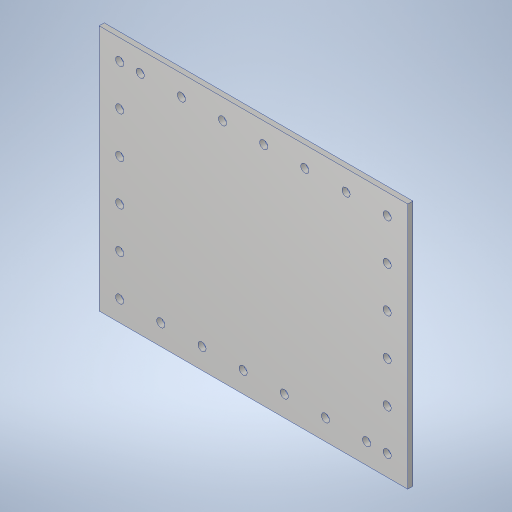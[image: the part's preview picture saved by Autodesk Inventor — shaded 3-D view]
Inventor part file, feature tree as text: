
AUTODESK INVENTOR PART (.ipt)
format: ipt  version: 2023.4 (Build 274418000, 418)  size: 269,824 bytes
history: native  units: in
note: dims shown in document units (in); Inventor stores cm internally (conversion verified against a paired STEP export)
features: pattern_linear x4, hole x2, extrude x1, sketch x1, projected_geometry x1
ambient origin geometry x8: Origin, YZ Plane, XZ Plane, XY Plane, X Axis, Y Axis, Z Axis, Center Point
bodies: Solid1 (feature_tree)
feature tree (9):
  extrude  "Extrusion1"  Depth=0.5in
  sketch  "Sketch2"  dims[d3=0.0in d4=0.5in d5=0.5in d6=0.201in d7=0.75in d8=0.385in d9=0.25in d10=0.5635in d11=1.0in d12=0.8108in d13=3.1496in d15=1.0in d16=2.7559in d18=1.0in d19=0.5in d20=0.5in d21=0.201in d22=0.75in d23=0.375in d24=0.25in d25=0.5635in d26=1.0in d27=0.8108in d28=2.7559in d30=1.0in d31=2.3622in d33=1.0in]
  hole  "Hole1"  [1 undecoded]
  pattern_linear  "Rectangular Pattern1"  Count1=8 Spacing1=1.0in
  pattern_linear  "Rectangular Pattern2"  Count1=7 Spacing1=1.0in
  hole  "Hole2"  [1 undecoded]
  pattern_linear  "Rectangular Pattern3"  Spacing1=0.5in  [1 undecoded]
  pattern_linear  "Rectangular Pattern4"  Count1=7 Spacing1=1.0in
  projected_geometry  "Project Cut Edges1"
note: 3 required parameter values undecoded (feature->parameter linkage not recoverable at this tier; creation-order binding heuristic only, values carry confidence <= 0.55)
